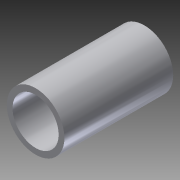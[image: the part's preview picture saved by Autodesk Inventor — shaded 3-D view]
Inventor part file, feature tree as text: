
AUTODESK INVENTOR PART (.ipt)
format: ipt  version: 2014 SP1 (Build 180222100, 222)  size: 86,016 bytes
history: native  units: in
note: dims shown in document units (in); Inventor stores cm internally (conversion verified against a paired STEP export)
features: extrude x1, sketch x1
ambient origin geometry x8: Origin, YZ Plane, XZ Plane, XY Plane, X Axis, Y Axis, Z Axis, Center Point
bodies: Solid1 (feature_tree)
feature tree (2):
  extrude  "Extrusion1"  Depth=1.18in
  sketch  "Sketch1"  dims[d0=0.5in d1=0.625in d2=1.18in d3=0.0in]
